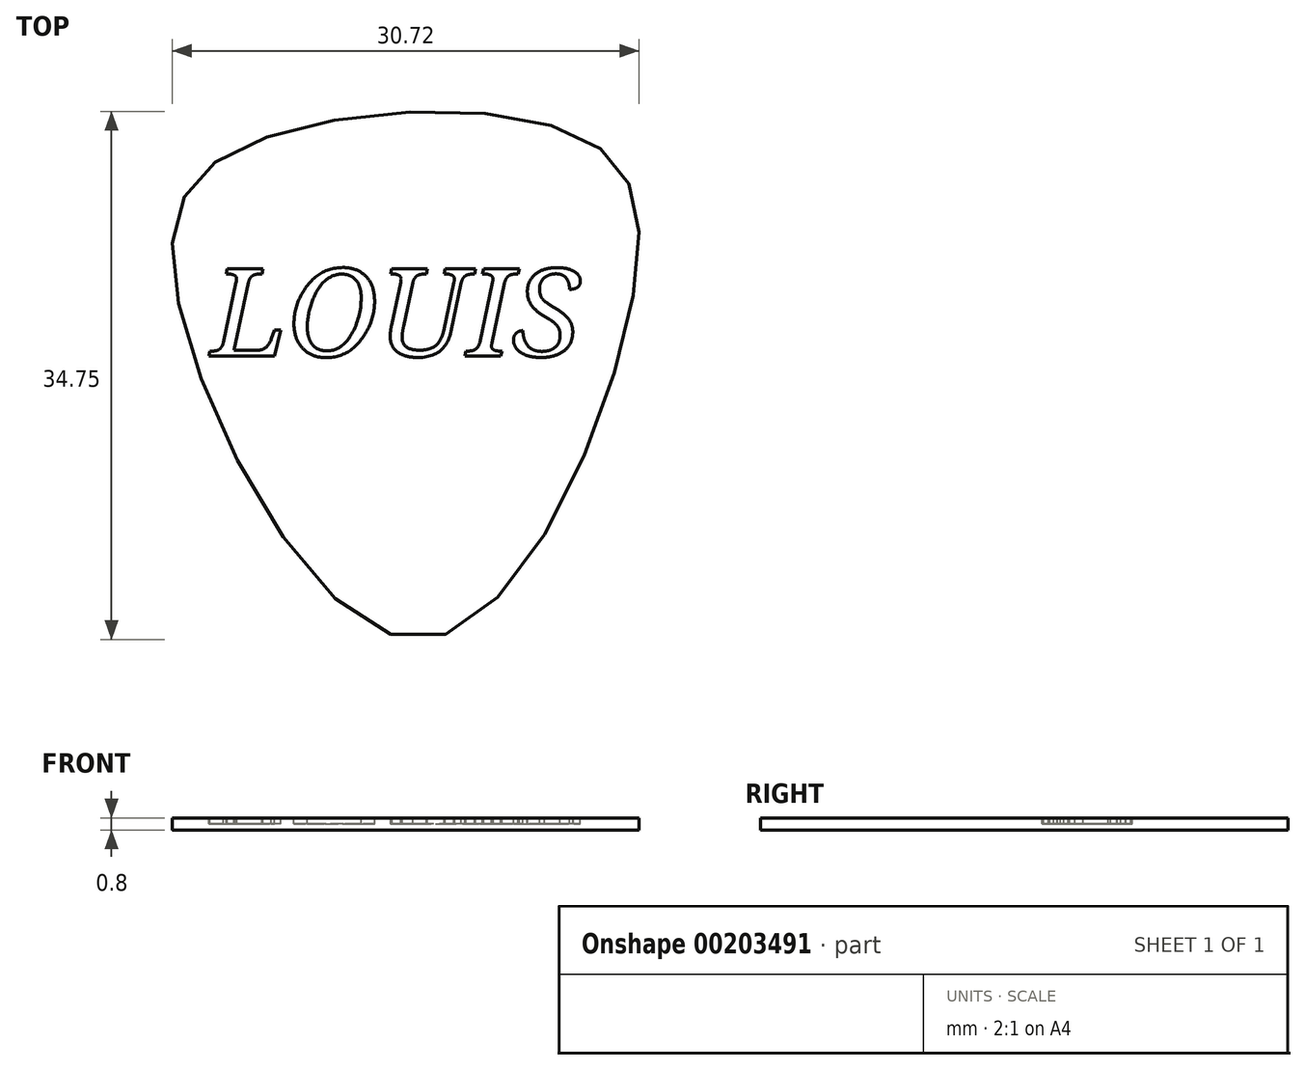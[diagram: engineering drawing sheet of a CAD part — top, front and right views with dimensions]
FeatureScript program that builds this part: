
annotation { "Feature Type Name" : "Feature", "Feature Type Description" : "" }
export const myFeature = defineFeature(function(context is Context, id is Id, definition is map)
    precondition{}
    {
        {
            var Q0;
            Q0=qCreatedBy(makeId("Top.planeOp"),FACE);
            var sketch = newSketch(context, id + "F0", { "sketchPlane" : qUnion([Q0])});
            skFitSpline(sketch, "E0", {"points": [v(-33.17, 24.66) * mm, v(-29.29, 34.82) * mm, v(-6.87, 35.71) * mm, v(-3.29, 24.95) * mm, v(-17.33, 2.54) * mm, v(-33.17, 24.66) * mm]});
            skSolve(sketch);
        }
        {
            var Q0;
            Q0 = qSketchRegion(id + "F0", true);
            extrude(context, id + "F1", {"entities" : qUnion([Q0]), "depth" : 0.8 * mm});
        }
        {
            var Q0;
            Q0=makeQuery(id+"F1.opExtrude","CAP_FACE",FACE,{"disambiguationData":[OSD([sQuery(id+"F0.wireOp",EDGE,"E0")])],"isStart":false});
            var sketch = newSketch(context, id + "F2", { "sketchPlane" : qUnion([Q0])});
            skText(sketch, "E1", { "text": "LOUIS", "fontName": "NotoSerif-Italic.ttf"});
            const initialGuessF2  = {"E1": [-0.03102, 0.02118, 1, 0, 0.0058]};
            skSetInitialGuess(sketch, initialGuessF2);
            skSolve(sketch);
        }
        {
            var Q0;
            Q0 = qSketchRegion(id + "F2", true);
            extrude(context, id + "F3", {"entities" : qUnion([Q0]), "operationType" : NewBodyOperationType.REMOVE, "oppositeDirection" : true, "depth" : 0.4 * mm});
        }
    });
